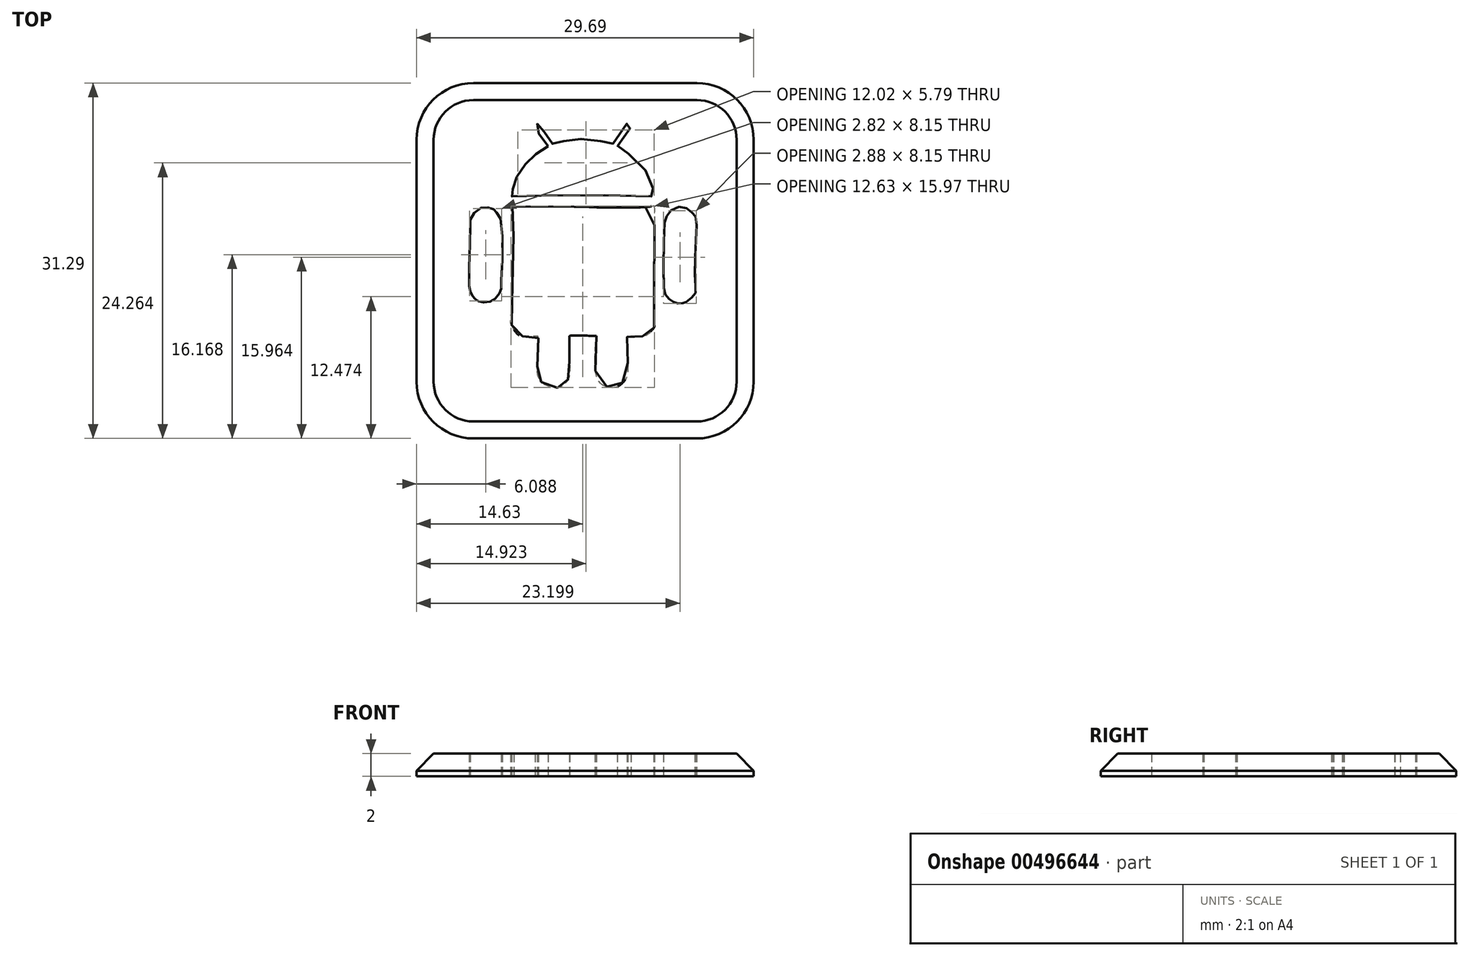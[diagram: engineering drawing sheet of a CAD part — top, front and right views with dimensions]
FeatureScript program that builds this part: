
annotation { "Feature Type Name" : "Feature", "Feature Type Description" : "" }
export const myFeature = defineFeature(function(context is Context, id is Id, definition is map)
    precondition{}
    {
        {
            var Q0;
            Q0=qCreatedBy(makeId("Top.planeOp"),FACE);
            var sketch = newSketch(context, id + "F0", { "sketchPlane" : qUnion([Q0])});
            skFitSpline(sketch, "E0", {"points": [v(6.96, 9.56) * mm, v(7.27, 9.15) * mm, v(7.6, 8.92) * mm, v(7.9, 8.8) * mm, v(8.1, 8.73) * mm, v(8.47, 8.77) * mm, v(8.65, 8.8) * mm, v(8.83, 8.9) * mm, v(9.36, 9.35) * mm, v(9.61, 9.73) * mm, v(9.59, 10.46) * mm, v(9.61, 13.76) * mm, v(9.65, 16.27) * mm, v(9.46, 16.6) * mm, v(9.1, 16.94) * mm, v(8.48, 17.25) * mm, v(7.55, 17.03) * mm, v(7.06, 16.44) * mm, v(6.88, 15.86) * mm, v(6.85, 9.87) * mm, v(6.96, 9.56) * mm]});
            skFitSpline(sketch, "E1", {"points": [v(-10.23, 9.83) * mm, v(-10.07, 9.46) * mm, v(-9.88, 9.2) * mm, v(-9.64, 9.02) * mm, v(-9.38, 8.9) * mm, v(-8.85, 8.85) * mm, v(-8.25, 9.02) * mm, v(-7.78, 9.48) * mm, v(-7.52, 10) * mm, v(-7.51, 10.18) * mm, v(-7.55, 16.14) * mm, v(-7.98, 16.83) * mm, v(-8.16, 17.03) * mm, v(-8.75, 17.2) * mm, v(-9.55, 17.05) * mm, v(-10.22, 16.15) * mm, v(-10.24, 15.87) * mm, v(-10.32, 10.12) * mm, v(-10.23, 9.83) * mm]});
            skFitSpline(sketch, "E2", {"points": [v(-3.39, 22.6) * mm, v(-4.18, 22.1) * mm, v(-5.1, 21.36) * mm, v(-5.7, 20.55) * mm, v(-6.3, 19.6) * mm, v(-6.48, 18.86) * mm, v(-6.55, 18.51) * mm, v(-6.58, 18.22) * mm, v(-6.17, 18.2) * mm, v(5.9, 18.15) * mm, v(6, 18.13) * mm, v(5.75, 19.3) * mm, v(4.78, 20.97) * mm, v(2.9, 22.45) * mm, v(2.73, 22.59) * mm, v(3.89, 24.25) * mm, v(3.89, 24.54) * mm, v(3.63, 24.64) * mm, v(2.3, 22.74) * mm, v(2.27, 22.73) * mm, v(0.73, 23.16) * mm, v(-0.9, 23.2) * mm, v(-2.35, 22.93) * mm, v(-2.93, 22.77) * mm, v(-3.16, 23.11) * mm, v(-3.97, 24.23) * mm, v(-4.23, 24.56) * mm, v(-4.43, 24.51) * mm, v(-4.51, 24.3) * mm, v(-3.48, 22.77) * mm, v(-3.39, 22.6) * mm]});
            skFitSpline(sketch, "E3", {"points": [v(-1.5, 5.85) * mm, v(-1.5, 3.85) * mm, v(-1.48, 2.52) * mm, v(-1.73, 1.87) * mm, v(-2.2, 1.44) * mm, v(-2.76, 1.34) * mm, v(-3.71, 1.63) * mm, v(-4.26, 2.33) * mm, v(-4.31, 3.04) * mm, v(-4.24, 5.64) * mm, v(-4.26, 5.87) * mm, v(-5.64, 5.87) * mm, v(-6.26, 6.27) * mm, v(-6.66, 7) * mm, v(-6.65, 7.58) * mm, v(-6.6, 16.96) * mm, v(-6.61, 17.28) * mm, v(5.71, 17.3) * mm, v(5.97, 17.3) * mm, v(5.98, 7.04) * mm, v(5.99, 6.69) * mm, v(5.56, 6.17) * mm, v(5.1, 5.9) * mm, v(3.87, 5.87) * mm, v(3.6, 5.83) * mm, v(3.57, 5.65) * mm, v(3.6, 2.58) * mm, v(3.24, 1.83) * mm, v(2.66, 1.4) * mm, v(1.6, 1.48) * mm, v(0.87, 2.4) * mm, v(0.88, 5.89) * mm], "startDerivative": vector(-1.38, -52.63) * mm, "endDerivative": vector(6.9, 77.46) * mm});
            skFitSpline(sketch, "E4", {"points": [v(0.88, 5.89) * mm, v(-1.5, 5.89) * mm, v(-1.5, 5.85) * mm], "startDerivative": vector(-3.87, 0.15) * mm, "endDerivative": vector(-0.1, -0.44) * mm});
            skLineSegment(sketch, "E5.bottom", {"start": v(-9.96, 28.16) * mm, "end": v(9.73, 28.16) * mm});
            skLineSegment(sketch, "E5.top", {"start": v(-9.96, -3.13) * mm, "end": v(9.73, -3.13) * mm});
            skLineSegment(sketch, "E5.left", {"start": v(-14.96, 23.16) * mm, "end": v(-14.96, 1.87) * mm});
            skLineSegment(sketch, "E5.right", {"start": v(14.73, 23.16) * mm, "end": v(14.73, 1.87) * mm});
            skPoint(sketch, "E6.visualSharp", {"position": v(-14.96, 28.16) * mm});
            skArc(sketch, "E6.filletArc", {"start": v(-9.96, 28.16) * mm, "mid": v(-13.5, 26.7) * mm, "end": v(-14.96, 23.16) * mm});
            skPoint(sketch, "E7.visualSharp", {"position": v(14.73, 28.16) * mm});
            skArc(sketch, "E7.filletArc", {"start": v(14.73, 23.16) * mm, "mid": v(13.26, 26.7) * mm, "end": v(9.73, 28.16) * mm});
            skPoint(sketch, "E8.visualSharp", {"position": v(14.73, -3.13) * mm});
            skArc(sketch, "E8.filletArc", {"start": v(9.73, -3.13) * mm, "mid": v(13.26, -1.67) * mm, "end": v(14.73, 1.87) * mm});
            skPoint(sketch, "E9.visualSharp", {"position": v(-14.96, -3.13) * mm});
            skArc(sketch, "E9.filletArc", {"start": v(-14.96, 1.87) * mm, "mid": v(-13.5, -1.67) * mm, "end": v(-9.96, -3.13) * mm});
            skSolve(sketch);
        }
        {
            var Q0;
            Q0=qSketchRegion(id+"F0",true);
            extrude(context, id + "F1", {"entities" : qUnion([Q0]), "depth" : 2 * mm, "offsetDistance" : 25 * mm});
        }
        {
            var Q0;
            Q0=makeQuery(id+"F1.opExtrude","CAP_EDGE",EDGE,{"disambiguationData":[OSD([sQuery(id+"F0.wireOp",EDGE,"E5.left")])],"isStart":false});
            chamfer(context, id + "F2", {"entities" : qUnion([Q0]), "width" : 1.5 * mm, "tangentPropagation" : true});
        }
    });
